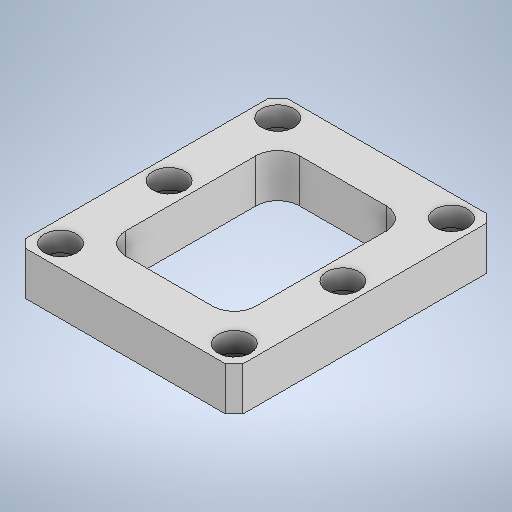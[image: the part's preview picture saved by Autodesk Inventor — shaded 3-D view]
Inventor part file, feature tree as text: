
AUTODESK INVENTOR PART (.ipt)
format: ipt  version: 2025.1 (Build 291241000, 241)  size: 304,128 bytes
history: native  units: mm
features: extrude x3, sketch x3, fillet x1, chamfer x1
ambient origin geometry x8: Origin, YZ Plane, XZ Plane, XY Plane, X Axis, Y Axis, Z Axis, Center Point
bodies: Solid1 (feature_tree)
feature tree (8):
  extrude  "Extrusion1"  Depth=120.0mm
  extrude  "Extrusion2"  Depth=80.0mm
  extrude  "Extrusion3"  Depth=9.0mm
  fillet  "Fillet1"  Radius=10.0mm
  chamfer  "Chamfer1"  Distance=50.0mm
  sketch  "Sketch1"  dims[d0=100.0mm d1=120.0mm]
  sketch  "Sketch2"  dims[d2=60.0mm d3=80.0mm]
  sketch  "Sketch3"  dims[d4=20.0mm d5=0.0mm d6=9.0mm d7=10.0mm d8=50.0mm d9=9.0mm d10=9.0mm d11=50.0mm d12=0.0mm d13=0.0mm d14=15.0mm d15=15.0mm d16=15.0mm d17=15.0mm d18=15.0mm d19=15.0mm d20=9.0mm d21=0.0mm d22=10.0mm d23=4.0mm d24=2.0mm d25=45.0deg]
